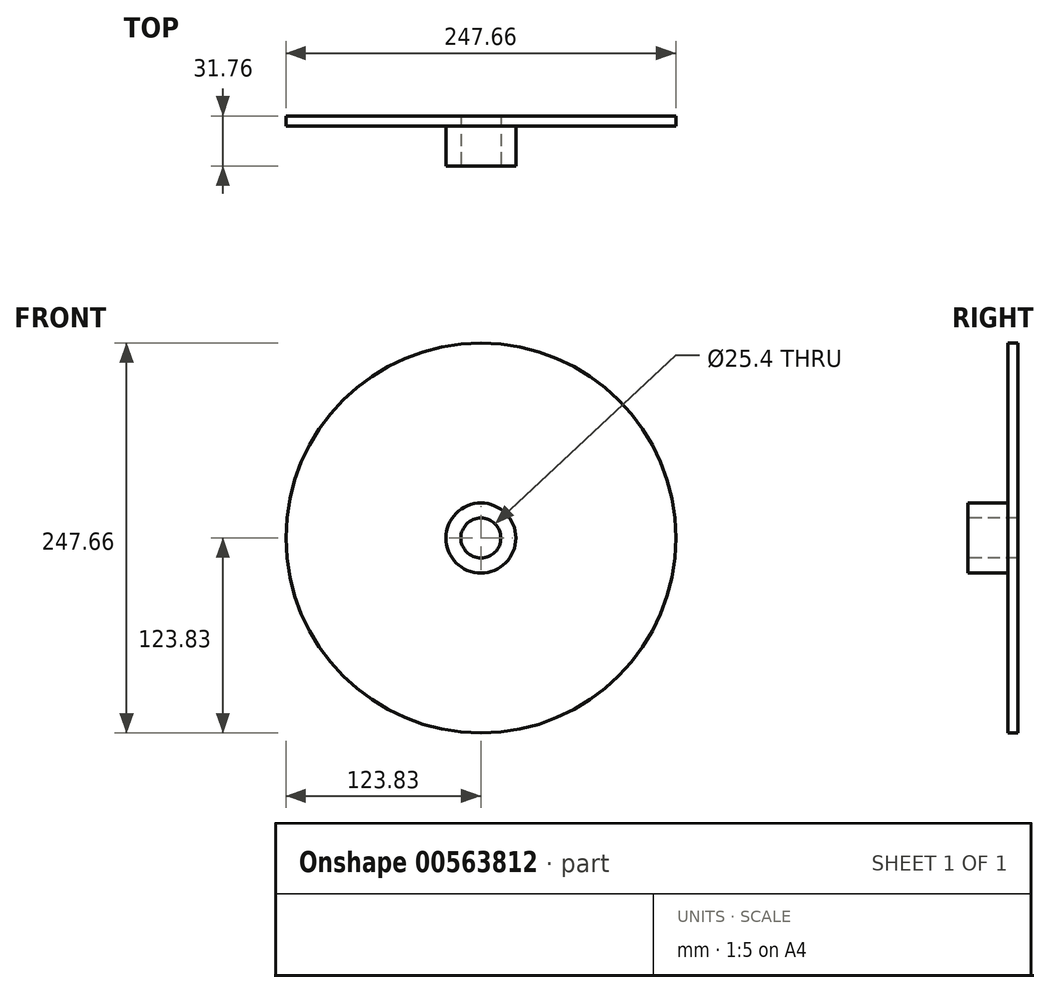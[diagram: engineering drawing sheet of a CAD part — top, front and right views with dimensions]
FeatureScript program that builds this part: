
annotation { "Feature Type Name" : "Feature", "Feature Type Description" : "" }
export const myFeature = defineFeature(function(context is Context, id is Id, definition is map)
    precondition{}
    {
        {
            var Q0;
            Q0=qCreatedBy(makeId("Front.planeOp"),FACE);
            var sketch = newSketch(context, id + "F0", { "sketchPlane" : qUnion([Q0])});
            skCircle(sketch, "E0", {"center": v(0, 0) * mm, "radius": 123.83 * mm});
            skSolve(sketch);
        }
        {
            var Q0;
            Q0=makeQuery(id+"F0.imprint","IMPRINT",FACE,{"disambiguationData":[TD([[makeQuery(id+"F0.imprint","IMPRINT",EDGE,{"derivedFrom":sQuery(id+"F0.wireOp",EDGE,"E0")}),1.0]])]});
            extrude(context, id + "F1", {"entities" : qUnion([Q0]), "endBound" : BoundingType.SYMMETRIC, "depth" : 6.35 * mm, "offsetDistance" : 25.4 * mm});
        }
        {
            var Q0;
            Q0=makeQuery(id+"F1.opExtrude","CAP_FACE",FACE,{"disambiguationData":[OSD([sQuery(id+"F0.wireOp",EDGE,"E0")])],"isStart":false});
            var sketch = newSketch(context, id + "F2", { "sketchPlane" : qUnion([Q0])});
            skCircle(sketch, "E1", {"center": v(0, 0) * mm, "radius": 22.23 * mm});
            skSolve(sketch);
        }
        {
            var Q0;
            Q0 = qSketchRegion(id + "F2", true);
            extrude(context, id + "F3", {"entities" : qUnion([Q0]), "operationType" : NewBodyOperationType.ADD, "depth" : 25.4 * mm, "offsetDistance" : 25.4 * mm});
        }
        {
            var Q0;
            Q0=makeQuery(id+"F3.opExtrude","CAP_FACE",FACE,{"disambiguationData":[OSD([sQuery(id+"F2.wireOp",EDGE,"E1")])],"isStart":false});
            var sketch = newSketch(context, id + "F4", { "sketchPlane" : qUnion([Q0])});
            skCircle(sketch, "E2", {"center": v(0, 0) * mm, "radius": 12.7 * mm});
            skSolve(sketch);
        }
        {
            var Q0;
            Q0 = qSketchRegion(id + "F4", true);
            extrude(context, id + "F5", {"entities" : qUnion([Q0]), "operationType" : NewBodyOperationType.REMOVE, "endBound" : BoundingType.SYMMETRIC, "oppositeDirection" : true, "depth" : 101.6 * mm, "offsetDistance" : 25.4 * mm});
        }
    });
